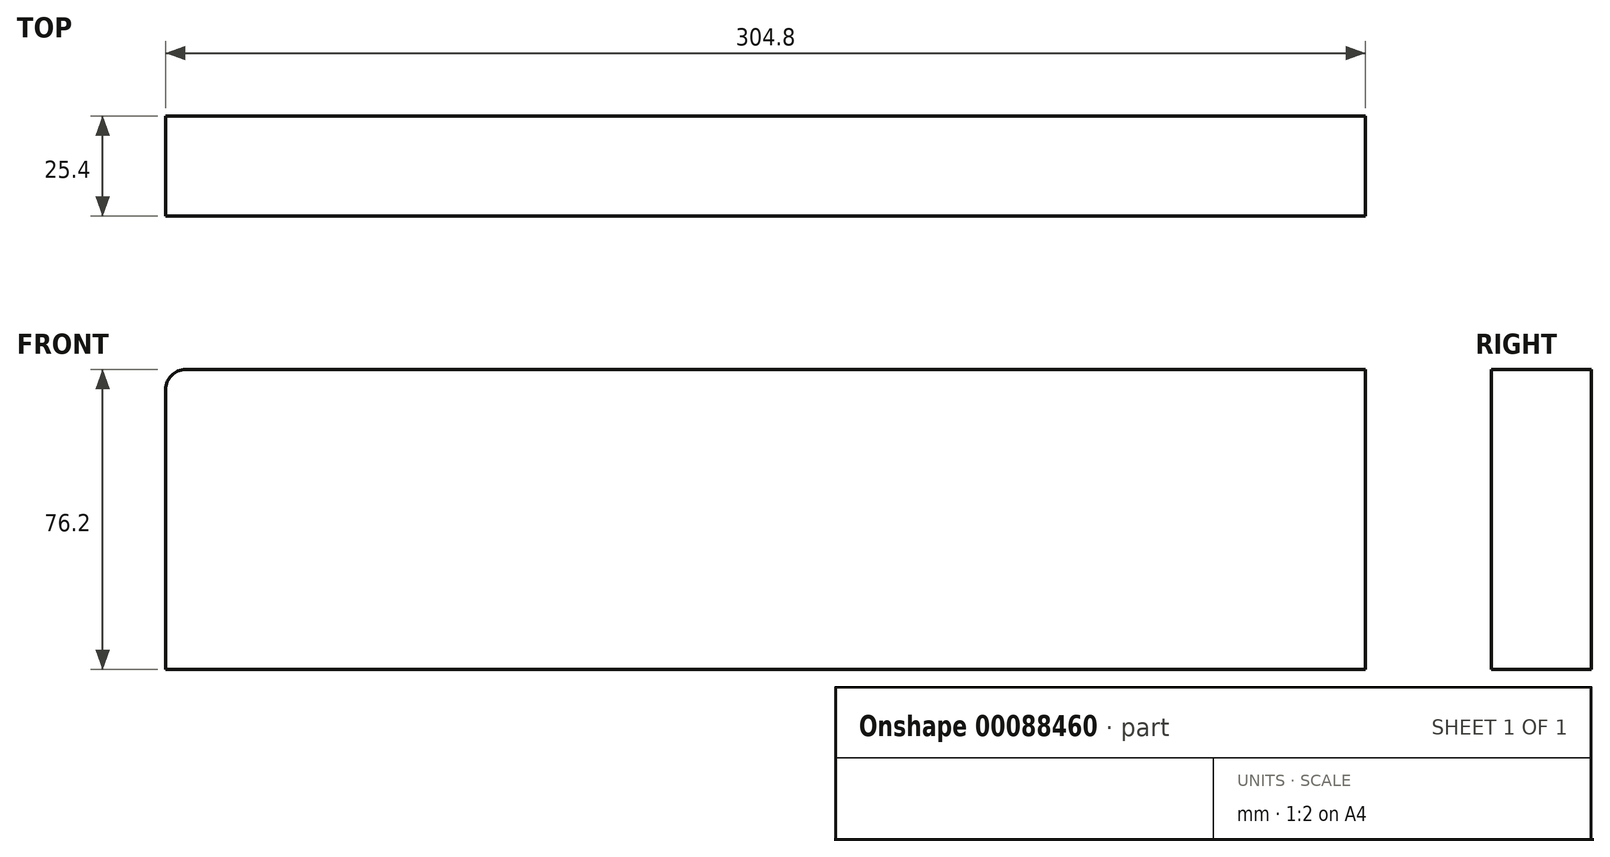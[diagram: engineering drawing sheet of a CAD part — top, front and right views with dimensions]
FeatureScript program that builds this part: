
annotation { "Feature Type Name" : "Feature", "Feature Type Description" : "" }
export const myFeature = defineFeature(function(context is Context, id is Id, definition is map)
    precondition{}
    {
        {
            var Q0;
            Q0=qCreatedBy(makeId("Front.planeOp"),FACE);
            var sketch = newSketch(context, id + "F0", { "sketchPlane" : qUnion([Q0])});
            skLineSegment(sketch, "E0.bottom", {"start": v(0, 0) * mm, "end": v(-304.8, 0) * mm});
            skLineSegment(sketch, "E0.top", {"start": v(0, 76.2) * mm, "end": v(-304.8, 76.2) * mm});
            skLineSegment(sketch, "E0.left", {"start": v(0, 0) * mm, "end": v(0, 76.2) * mm});
            skLineSegment(sketch, "E0.right", {"start": v(-304.8, 0) * mm, "end": v(-304.8, 76.2) * mm});
            skSolve(sketch);
        }
        {
            var Q0;
            Q0=makeQuery(id+"F0.imprint","IMPRINT",FACE,{"disambiguationData":[TD([[makeQuery(id+"F0.imprint","IMPRINT",EDGE,{"derivedFrom":sQuery(id+"F0.wireOp",EDGE,"E0.bottom")}),-1.0]])]});
            extrude(context, id + "F1", {"entities" : qUnion([Q0]), "depth" : 25.4 * mm});
        }
        {
            var Q0;
            Q0=makeQuery(id+"F1.opExtrude","SWEPT_EDGE",EDGE,{"disambiguationData":[OSD([sQuery(id+"F0.wireOp",EDGE,"E0.top"),sQuery(id+"F0.wireOp",EDGE,"E0.right")])]});
            fillet(context, id + "F2", {"entities" : qUnion([Q0]), "radius" : 5.08 * mm, "tangentPropagation" : true, "allowEdgeOverflow" : false});
        }
    });
